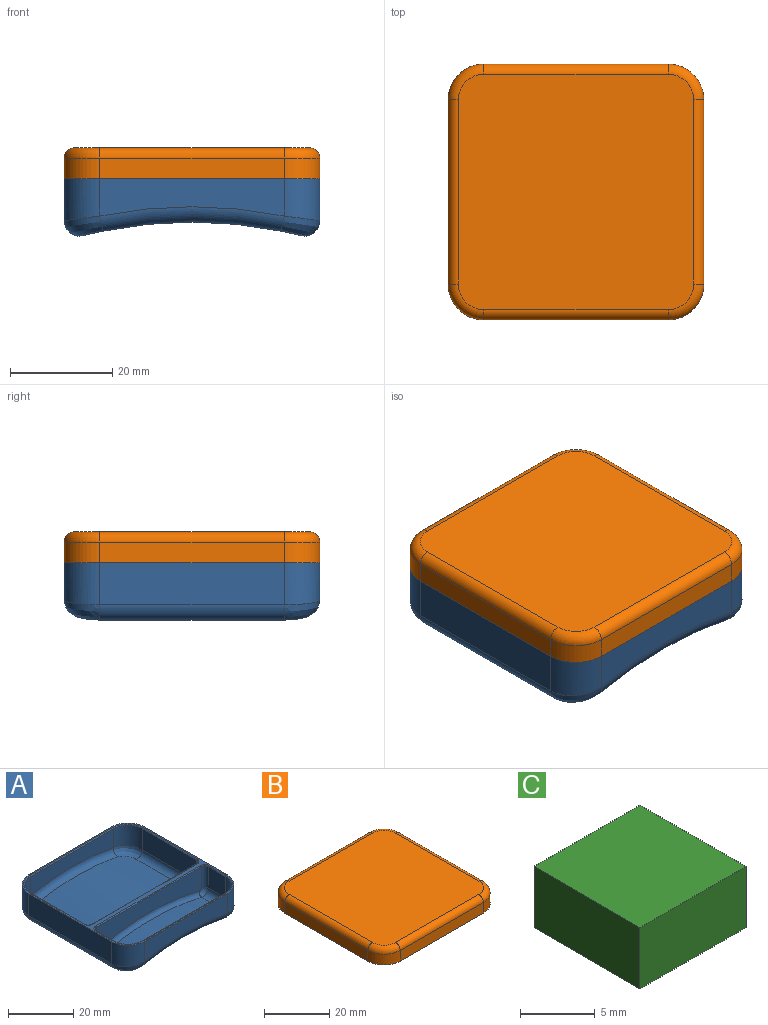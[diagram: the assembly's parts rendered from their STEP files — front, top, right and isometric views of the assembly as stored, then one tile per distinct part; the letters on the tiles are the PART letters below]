
ASSEMBLY  parts=3 mates=5
PART A: 68 faces, bbox 50.5x50.5x16.3 mm
  f0: plane 23.5x7.95mm, normal (-1,0,0), area 186.8mm2, adj f4,f33,f42,f67
  f1: plane 23.5x7.95mm, normal (1,0,0), area 186.8mm2, adj f3,f36,f46,f60
  f2: cylinder r=87.3mm len=42.92mm, axis (0,-1,0), area 1185.6mm2, adj f3,f4,f25,f28,f31,f44
  f3: cylinder r=2.2mm len=23.5mm, axis (0,-1,0), area 94.1mm2, adj f1,f2,f28,f45
  f4: cylinder r=2.2mm len=23.5mm, axis (0,-1,0), area 94.1mm2, adj f0,f2,f31,f43
  f5: plane 50x50mm, normal (0,0,1), area 164.6mm2, adj f15,f16,f17,f18,f19,f20,f21,f22
  f6: cylinder r=86.5mm len=44mm, axis (0,-1,0), area 1876.8mm2, adj f7,f8,f9,f10,f11,f12,f13,f14
  f7: torus R=89.5mm, axis (0,1,0), area 167.2mm2, adj f6,f12,f13,f22
  f8: torus R=89.5mm, axis (0,1,0), area 167.2mm2, adj f6,f11,f14,f21
  f9: cylinder r=3mm len=36mm, axis (0,-1,0), area 196.5mm2, adj f6,f11,f12,f20
  f10: cylinder r=3mm len=36mm, axis (0,-1,0), area 196.5mm2, adj f6,f13,f14,f17
  f11: bspline ~9.1x8.78mm, area 48.8mm2, adj f6,f8,f9,f19
  f12: bspline ~9.1x8.77mm, area 48.8mm2, adj f6,f7,f9,f18
  f13: bspline ~9.1x8.78mm, area 48.8mm2, adj f6,f7,f10,f15
  f14: bspline ~9.1x8.77mm, area 48.8mm2, adj f6,f8,f10,f16
  f15: cylinder r=7mm len=8.25mm, axis (0,0,1), area 86.9mm2, adj f5,f13,f17,f22
  f16: cylinder r=7mm len=8.25mm, axis (0,0,-1), area 86.9mm2, adj f5,f14,f17,f21
  f17: plane 36x8.25mm, normal (1,0,0), area 297mm2, adj f5,f10,f15,f16
  f18: cylinder r=7mm len=8.25mm, axis (0,0,-1), area 86.9mm2, adj f5,f12,f20,f22
  f19: cylinder r=7mm len=8.25mm, axis (0,0,1), area 86.9mm2, adj f5,f11,f20,f21
  f20: plane 36x8.25mm, normal (-1,0,0), area 297mm2, adj f5,f9,f18,f19
  f21: plane 36x7.33mm, normal (0,1,0), area 220mm2, adj f5,f8,f16,f19
  f22: plane 36x7.33mm, normal (0,-1,0), area 220mm2, adj f5,f7,f15,f18
  f23: cylinder r=87.3mm len=42.92mm, axis (0,-1,0), area 491.8mm2, adj f24,f26,f27,f29,f30,f49
  f24: torus R=89.5mm, axis (0,1,0), area 123.3mm2, adj f23,f29,f30,f39
  f25: torus R=89.5mm, axis (0,1,0), area 123.3mm2, adj f2,f28,f31,f38
  f26: cylinder r=2.2mm len=7.5mm, axis (0,-1,0), area 30mm2, adj f23,f29,f37,f50
  f27: cylinder r=2.2mm len=7.5mm, axis (0,-1,0), area 30mm2, adj f23,f30,f34,f48
  f28: bspline ~7.98x7.73mm, area 32.7mm2, adj f2,f3,f25,f36
  f29: bspline ~7.98x7.73mm, area 32.7mm2, adj f23,f24,f26,f35
  f30: bspline ~7.98x7.73mm, area 32.7mm2, adj f23,f24,f27,f32
  f31: bspline ~7.98x7.73mm, area 32.7mm2, adj f2,f4,f25,f33
  f32: cylinder r=6.2mm len=7.95mm, axis (0,0,1), area 74.1mm2, adj f30,f34,f39,f58
  f33: cylinder r=6.2mm len=7.95mm, axis (0,0,-1), area 74.1mm2, adj f0,f31,f38,f65
  f34: plane 7.95x7.5mm, normal (-1,0,0), area 59.6mm2, adj f27,f32,f47,f59
  f35: cylinder r=6.2mm len=7.95mm, axis (0,0,-1), area 74.1mm2, adj f29,f37,f39,f54
  f36: cylinder r=6.2mm len=7.95mm, axis (0,0,1), area 74.1mm2, adj f1,f28,f38,f61
  f37: plane 7.95x7.5mm, normal (1,0,0), area 59.6mm2, adj f26,f35,f51,f52
  f38: plane 36x7.03mm, normal (0,-1,0), area 209.2mm2, adj f25,f33,f36,f63
  f39: plane 36x7.03mm, normal (0,1,0), area 209.2mm2, adj f24,f32,f35,f56
  f40: plane 45.4x8.65mm, normal (0,-1,0), area 312.1mm2, adj f47,f48,f49,f50,f51,f55
  f41: plane 45.4x8.65mm, normal (0,1,0), area 312.1mm2, adj f42,f43,f44,f45,f46,f64
  f42: cylinder r=1.5mm len=7.95mm, axis (0,0,-1), area 18.7mm2, adj f0,f41,f43,f66
  f43: torus R=0.7mm, axis (0,1,0), area 7.1mm2, adj f4,f41,f42,f44
  f44: torus R=88.8mm, axis (0,1,0), area 102.8mm2, adj f2,f41,f43,f45
  f45: torus R=0.7mm, axis (0,1,0), area 7.1mm2, adj f3,f41,f44,f46
  f46: cylinder r=1.5mm len=7.95mm, axis (0,0,1), area 18.7mm2, adj f1,f41,f45,f62
  f47: cylinder r=1.5mm len=7.95mm, axis (0,0,1), area 18.7mm2, adj f34,f40,f48,f57
  f48: torus R=0.7mm, axis (0,1,0), area 7.1mm2, adj f27,f40,f47,f49
  f49: torus R=88.8mm, axis (0,1,0), area 102.8mm2, adj f23,f40,f48,f50
  f50: torus R=0.7mm, axis (0,1,0), area 7.1mm2, adj f26,f40,f49,f51
  f51: cylinder r=1.5mm len=7.95mm, axis (0,0,-1), area 18.7mm2, adj f37,f40,f50,f53
  f52: cylinder r=0.3mm len=7.5mm, axis (0,-1,0), area 3.5mm2, adj f5,f37,f53,f54
  f53: torus R=1.8mm, axis (0,0,1), area 1.2mm2, adj f5,f51,f52,f55
  f54: torus R=6.5mm, axis (0,0,1), area 4.7mm2, adj f5,f35,f52,f56
  f55: cylinder r=0.3mm len=45.4mm, axis (-1,0,0), area 21.4mm2, adj f5,f40,f53,f57
  f56: cylinder r=0.3mm len=36mm, axis (1,0,0), area 17mm2, adj f5,f39,f54,f58
  f57: torus R=1.8mm, axis (0,0,1), area 1.2mm2, adj f5,f47,f55,f59
  f58: torus R=6.5mm, axis (0,0,1), area 4.7mm2, adj f5,f32,f56,f59
  f59: cylinder r=0.3mm len=7.5mm, axis (0,1,0), area 3.5mm2, adj f5,f34,f57,f58
  f60: cylinder r=0.3mm len=23.5mm, axis (0,-1,0), area 11.1mm2, adj f1,f5,f61,f62
  f61: torus R=6.5mm, axis (0,0,1), area 4.7mm2, adj f5,f36,f60,f63
  f62: torus R=1.8mm, axis (0,0,1), area 1.2mm2, adj f5,f46,f60,f64
  f63: cylinder r=0.3mm len=36mm, axis (-1,0,0), area 17mm2, adj f5,f38,f61,f65
  f64: cylinder r=0.3mm len=45.4mm, axis (1,0,0), area 21.4mm2, adj f5,f41,f62,f66
  f65: torus R=6.5mm, axis (0,0,1), area 4.7mm2, adj f5,f33,f63,f67
  f66: torus R=1.8mm, axis (0,0,1), area 1.2mm2, adj f5,f42,f64,f67
  f67: cylinder r=0.3mm len=23.5mm, axis (0,1,0), area 11.1mm2, adj f0,f5,f65,f66
PART B: 99 faces, bbox 51.2x51.2x6 mm
  f0: plane 19.51x3.7mm, normal (0,1,0), area 72.2mm2, adj f19,f24,f94,f97
  f1: plane 7.42x3.7mm, normal (0,1,0), area 27.5mm2, adj f25,f55,f60,f96
  f2: plane 19.51x3.7mm, normal (0,-1,0), area 72.2mm2, adj f21,f30,f81,f82
  f3: plane 7.42x3.7mm, normal (0,-1,0), area 27.5mm2, adj f31,f54,f63,f83
  f4: plane 15x3.7mm, normal (1,0,0), area 55.5mm2, adj f23,f26,f76,f87
  f5: plane 9.5x3.7mm, normal (1,0,0), area 35.1mm2, adj f27,f54,f64,f86
  f6: plane 15x3.7mm, normal (-1,0,0), area 55.5mm2, adj f17,f28,f79,f85
  f7: plane 9.5x3.7mm, normal (-1,0,0), area 35.1mm2, adj f29,f57,f59,f84
  f8: plane 14.5x12.42mm, normal (0,0,-1), area 174.8mm2, adj f22,f60,f62,f74,f96
  f9: plane 19.51x14.5mm, normal (0,0,-1), area 282.9mm2, adj f19,f75,f94,f97
  f10: plane 14.5x12.07mm, normal (0,0,-1), area 169.6mm2, adj f16,f18,f58,f78,f95
  f11: plane 15x12.07mm, normal (0,0,-1), area 181mm2, adj f17,f79,f85,f90
  f12: plane 14.5x12.07mm, normal (0,0,-1), area 169.6mm2, adj f20,f59,f61,f80,f84
  f13: plane 19.51x14.5mm, normal (0,0,-1), area 282.9mm2, adj f21,f81,f82,f88
  f14: plane 15x12.42mm, normal (0,0,-1), area 186.3mm2, adj f23,f76,f87,f93
  f15: plane 14.5x12.42mm, normal (0,0,-1), area 174.8mm2, adj f63,f64,f65,f83,f86
  f16: cylinder r=1.2mm len=9.5mm, axis (0,-1,0), area 17.9mm2, adj f10,f53,f58,f78
  f17: cylinder r=1.2mm len=15mm, axis (0,-1,0), area 28.3mm2, adj f6,f11,f79,f85
  f18: cylinder r=1.2mm len=7.07mm, axis (-1,0,0), area 13.3mm2, adj f10,f50,f58,f95
  f19: cylinder r=1.2mm len=19.51mm, axis (-1,0,0), area 36.8mm2, adj f0,f9,f94,f97
  f20: cylinder r=1.2mm len=7.07mm, axis (1,0,0), area 13.3mm2, adj f12,f51,f61,f80
  f21: cylinder r=1.2mm len=19.51mm, axis (1,0,0), area 36.8mm2, adj f2,f13,f81,f82
  f22: cylinder r=1.2mm len=9.5mm, axis (0,1,0), area 17.9mm2, adj f8,f52,f62,f74
  f23: cylinder r=1.2mm len=15mm, axis (0,1,0), area 28.3mm2, adj f4,f14,f76,f87
  f24: cylinder r=0.3mm len=19.51mm, axis (-1,0,0), area 9.2mm2, adj f0,f32,f94,f97
  f25: cylinder r=0.3mm len=7.42mm, axis (-1,0,0), area 3.5mm2, adj f1,f32,f67,f96
  f26: cylinder r=0.3mm len=15mm, axis (0,1,0), area 7.1mm2, adj f4,f32,f76,f87
  f27: cylinder r=0.3mm len=9.5mm, axis (0,1,0), area 4.5mm2, adj f5,f32,f71,f86
  f28: cylinder r=0.3mm len=15mm, axis (0,-1,0), area 7.1mm2, adj f6,f32,f79,f85
  f29: cylinder r=0.3mm len=9.5mm, axis (0,-1,0), area 4.5mm2, adj f7,f32,f72,f84
  f30: cylinder r=0.3mm len=19.51mm, axis (1,0,0), area 9.2mm2, adj f2,f32,f81,f82
  f31: cylinder r=0.3mm len=7.42mm, axis (1,0,0), area 3.5mm2, adj f3,f32,f71,f83
  f32: plane 50x50mm, normal (0,0,-1), area 285.2mm2, adj f24,f25,f26,f27,f28,f29,f30,f31
  f33: plane 36x4mm, normal (0,-1,0), area 144mm2, adj f32,f39,f40,f44
  f34: plane 36x4mm, normal (0,1,0), area 144mm2, adj f32,f38,f41,f47
  f35: plane 36x4mm, normal (-1,0,0), area 144mm2, adj f32,f38,f39,f48
  f36: plane 36x4mm, normal (1,0,0), area 144mm2, adj f32,f40,f41,f43
  f37: plane 46x46mm, normal (0,0,1), area 2094.5mm2, adj f42,f43,f44,f45,f46,f47,f48,f49
  f38: cylinder r=7mm len=7mm, axis (0,0,1), area 44mm2, adj f32,f34,f35,f49
  f39: cylinder r=7mm len=7mm, axis (0,0,-1), area 44mm2, adj f32,f33,f35,f46
  f40: cylinder r=7mm len=7mm, axis (0,0,1), area 44mm2, adj f32,f33,f36,f42
  f41: cylinder r=7mm len=7mm, axis (0,0,-1), area 44mm2, adj f32,f34,f36,f45
  f42: torus R=5mm, axis (0,0,1), area 31mm2, adj f37,f40,f43,f44
  f43: cylinder r=2mm len=36mm, axis (0,-1,0), area 113.1mm2, adj f36,f37,f42,f45
  f44: cylinder r=2mm len=36mm, axis (-1,0,0), area 113.1mm2, adj f33,f37,f42,f46
  f45: torus R=5mm, axis (0,0,1), area 31mm2, adj f37,f41,f43,f47
  f46: torus R=5mm, axis (0,0,1), area 31mm2, adj f37,f39,f44,f48
  f47: cylinder r=2mm len=36mm, axis (1,0,0), area 113.1mm2, adj f34,f37,f45,f49
  f48: cylinder r=2mm len=36mm, axis (0,1,0), area 113.1mm2, adj f35,f37,f46,f49
  f49: torus R=5mm, axis (0,0,1), area 31mm2, adj f37,f38,f47,f48
  f50: plane 7.07x3.7mm, normal (0,1,0), area 26.2mm2, adj f18,f56,f66,f95
  f51: plane 7.07x3.7mm, normal (0,-1,0), area 26.2mm2, adj f20,f57,f73,f80
  f52: plane 9.5x3.7mm, normal (1,0,0), area 35.1mm2, adj f22,f55,f69,f74
  f53: plane 9.5x3.7mm, normal (-1,0,0), area 35.1mm2, adj f16,f56,f70,f78
  f54: cylinder r=6.2mm len=6.2mm, axis (0,0,1), area 36mm2, adj f3,f5,f65,f71
  f55: cylinder r=6.2mm len=6.2mm, axis (0,0,-1), area 36mm2, adj f1,f52,f62,f67
  f56: cylinder r=6.2mm len=6.2mm, axis (0,0,1), area 36mm2, adj f50,f53,f58,f68
  f57: cylinder r=6.2mm len=6.2mm, axis (0,0,-1), area 36mm2, adj f7,f51,f61,f72
  f58: torus R=5mm, axis (0,0,1), area 17.1mm2, adj f10,f16,f18,f56
  f59: cylinder r=1.2mm len=9.5mm, axis (0,-1,0), area 17.9mm2, adj f7,f12,f61,f84
  f60: cylinder r=1.2mm len=7.42mm, axis (-1,0,0), area 14mm2, adj f1,f8,f62,f96
  f61: torus R=5mm, axis (0,0,1), area 17.1mm2, adj f12,f20,f57,f59
  f62: torus R=5mm, axis (0,0,1), area 17.1mm2, adj f8,f22,f55,f60
  f63: cylinder r=1.2mm len=7.42mm, axis (1,0,0), area 14mm2, adj f3,f15,f65,f83
  f64: cylinder r=1.2mm len=9.5mm, axis (0,1,0), area 17.9mm2, adj f5,f15,f65,f86
  f65: torus R=5mm, axis (0,0,1), area 17.1mm2, adj f15,f54,f63,f64
  f66: cylinder r=0.3mm len=7.07mm, axis (-1,0,0), area 3.3mm2, adj f32,f50,f68,f95
  f67: torus R=6.5mm, axis (0,0,1), area 4.7mm2, adj f25,f32,f55,f69
  f68: torus R=6.5mm, axis (0,0,1), area 4.7mm2, adj f32,f56,f66,f70
  f69: cylinder r=0.3mm len=9.5mm, axis (0,1,0), area 4.5mm2, adj f32,f52,f67,f74
  f70: cylinder r=0.3mm len=9.5mm, axis (0,-1,0), area 4.5mm2, adj f32,f53,f68,f78
  f71: torus R=6.5mm, axis (0,0,1), area 4.7mm2, adj f27,f31,f32,f54
  f72: torus R=6.5mm, axis (0,0,1), area 4.7mm2, adj f29,f32,f57,f73
  f73: cylinder r=0.3mm len=7.07mm, axis (1,0,0), area 3.3mm2, adj f32,f51,f72,f80
  f74: plane 13.92x5.2mm, normal (0,-1,0), area 70.5mm2, adj f8,f22,f32,f52,f69,f96
  f75: plane 19.51x5.2mm, normal (0,-1,0), area 101.4mm2, adj f9,f32,f94,f97
  f76: plane 13.92x5.2mm, normal (0,1,0), area 70.5mm2, adj f4,f14,f23,f26,f32,f93
  f77: plane 19.51x5.2mm, normal (0,1,0), area 101.4mm2, adj f32,f91,f92,f98
  f78: plane 13.57x5.2mm, normal (0,-1,0), area 68.7mm2, adj f10,f16,f32,f53,f70,f95
  f79: plane 13.57x5.2mm, normal (0,1,0), area 68.7mm2, adj f6,f11,f17,f28,f32,f90
  f80: plane 16x5.2mm, normal (1,0,0), area 81.4mm2, adj f12,f20,f32,f51,f73,f84
  f81: plane 16x5.2mm, normal (-1,0,0), area 81.4mm2, adj f2,f13,f21,f30,f32,f88
  f82: plane 16x5.2mm, normal (1,0,0), area 81.4mm2, adj f2,f13,f21,f30,f32,f88
  f83: plane 16x5.2mm, normal (-1,0,0), area 81.4mm2, adj f3,f15,f31,f32,f63,f86
  f84: plane 13.57x5.2mm, normal (0,1,0), area 68.7mm2, adj f7,f12,f29,f32,f59,f80
  f85: plane 13.57x5.2mm, normal (0,-1,0), area 68.7mm2, adj f6,f11,f17,f28,f32,f90
  f86: plane 13.92x5.2mm, normal (0,1,0), area 70.5mm2, adj f5,f15,f27,f32,f64,f83
  f87: plane 13.92x5.2mm, normal (0,-1,0), area 70.5mm2, adj f4,f14,f23,f26,f32,f93
  f88: plane 19.51x5.2mm, normal (0,1,0), area 101.4mm2, adj f13,f32,f81,f82
  f89: plane 19.51x5.2mm, normal (0,-1,0), area 101.4mm2, adj f32,f91,f92,f98
  f90: plane 15x5.2mm, normal (1,0,0), area 78mm2, adj f11,f32,f79,f85
  f91: plane 15x5.2mm, normal (-1,0,0), area 78mm2, adj f32,f77,f89,f98
  f92: plane 15x5.2mm, normal (1,0,0), area 78mm2, adj f32,f77,f89,f98
  f93: plane 15x5.2mm, normal (-1,0,0), area 78mm2, adj f14,f32,f76,f87
  f94: plane 16x5.2mm, normal (-1,0,0), area 81.4mm2, adj f0,f9,f19,f24,f32,f75
  f95: plane 16x5.2mm, normal (1,0,0), area 81.4mm2, adj f10,f18,f32,f50,f66,f78
  f96: plane 16x5.2mm, normal (-1,0,0), area 81.4mm2, adj f1,f8,f25,f32,f60,f74
  f97: plane 16x5.2mm, normal (1,0,0), area 81.4mm2, adj f0,f9,f19,f24,f32,f75
  f98: plane 19.51x15mm, normal (0,0,-1), area 292.6mm2, adj f77,f89,f91,f92
PART C: 6 faces, bbox 10x10x5 mm
  f0: plane 10x5mm, normal (0,1,0), area 50mm2, adj f1,f3,f4,f5
  f1: plane 10x5mm, normal (-1,0,0), area 50mm2, adj f0,f2,f4,f5
  f2: plane 10x5mm, normal (0,-1,0), area 50mm2, adj f1,f3,f4,f5
  f3: plane 10x5mm, normal (1,0,0), area 50mm2, adj f0,f2,f4,f5
  f4: plane 10x10mm, normal (0,0,1), area 100mm2, adj f0,f1,f2,f3
  f5: plane 10x10mm, normal (0,0,-1), area 100mm2, adj f0,f1,f2,f3
PLACE A rot(axis=(0,1,0),0deg) t=(1.86,2.38,-10.1)mm
PLACE B t=(1.86,2.38,-10.1)mm
PLACE C rot(axis=(0,1,0),0deg) t=(-56.41,-8.98,-0.1)mm
MATE planar A.f20 <-> B.f35  axis (-1,0,0) through (-23.14,2.38,0.77)mm
MATE planar A.f41 <-> C.f2  axis (0,1,0) through (1.86,-4.62,1.1)mm
MATE planar B.f33 <-> A.f22  axis (0,-1,0) through (1.86,-22.62,6.9)mm
MATE planar A.f5 <-> B.f32  axis (0,0,1) through (-16.14,-22.12,4.9)mm
MATE planar C.f4 <-> A.f5  axis (0,0,1) through (1.86,0.38,4.9)mm
